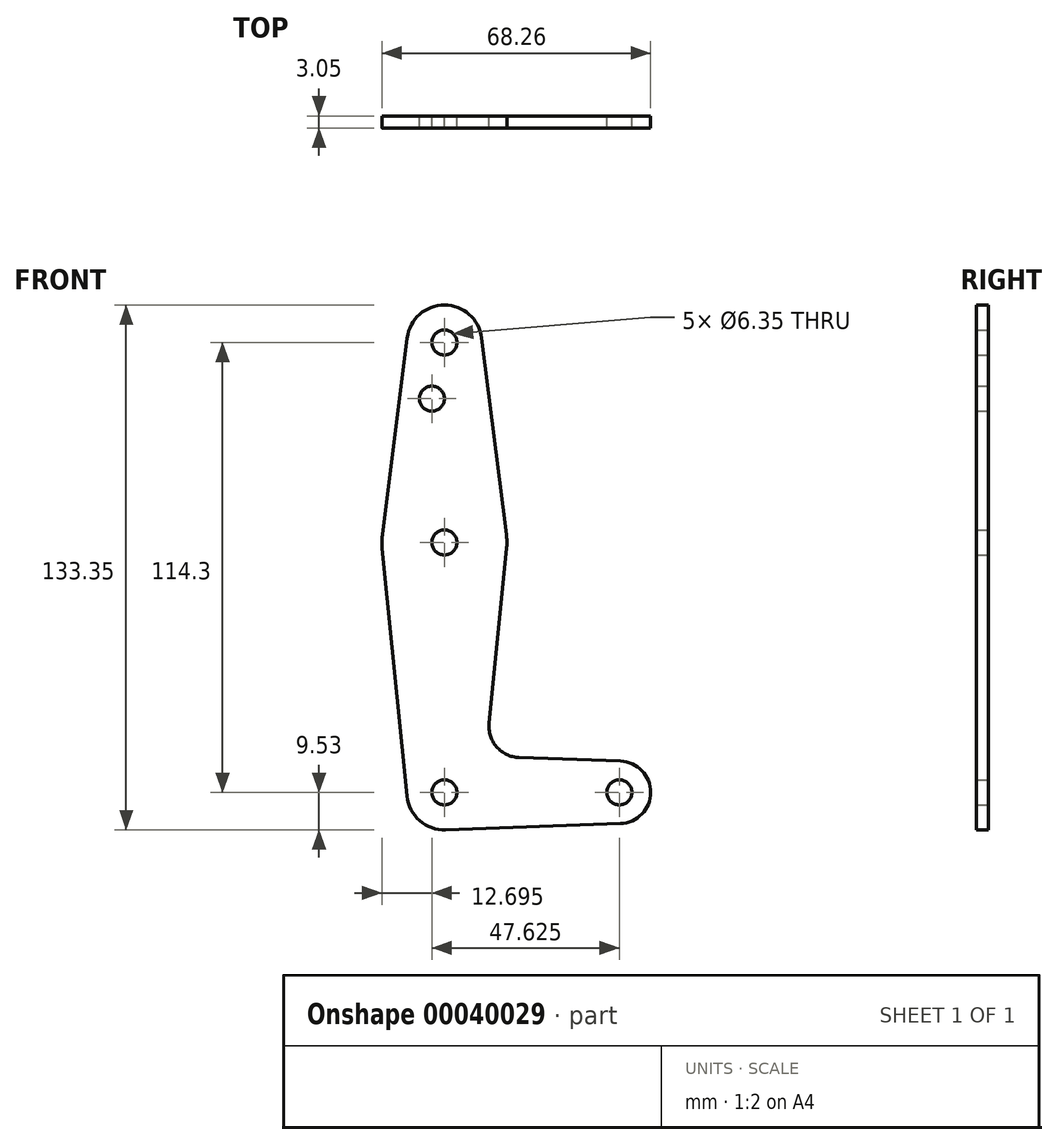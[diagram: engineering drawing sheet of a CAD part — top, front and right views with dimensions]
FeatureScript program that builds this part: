
annotation { "Feature Type Name" : "Feature", "Feature Type Description" : "" }
export const myFeature = defineFeature(function(context is Context, id is Id, definition is map)
    precondition{}
    {
        {
            var Q0;
            Q0=qCreatedBy(makeId("Front.planeOp"),FACE);
            var sketch = newSketch(context, id + "F0", { "sketchPlane" : qUnion([Q0])});
            skLineSegment(sketch, "E0", {"start": v(0, 50.8) * mm, "end": v(0, -63.5) * mm, "construction": true});
            skCircle(sketch, "E1", {"center": v(0, 50.8) * mm, "radius": 9.53 * mm});
            skCircle(sketch, "E2", {"center": v(0, 0) * mm, "radius": 15.88 * mm});
            skCircle(sketch, "E3", {"center": v(0, -63.5) * mm, "radius": 9.53 * mm});
            skLineSegment(sketch, "E4", {"start": v(0, -63.5) * mm, "end": v(44.45, -63.5) * mm, "construction": true});
            skCircle(sketch, "E5", {"center": v(44.45, -63.5) * mm, "radius": 7.94 * mm});
            skLineSegment(sketch, "E6", {"start": v(-9.45, 52) * mm, "end": v(-15.75, 1.98) * mm});
            skLineSegment(sketch, "E7", {"start": v(9.45, 52) * mm, "end": v(15.75, 1.98) * mm});
            skLineSegment(sketch, "E8", {"start": v(-15.8, -1.59) * mm, "end": v(-9.48, -64.45) * mm});
            skLineSegment(sketch, "E9", {"start": v(15.8, -1.59) * mm, "end": v(11.34, -45.9) * mm});
            skLineSegment(sketch, "E10", {"start": v(18.97, -54.65) * mm, "end": v(44.73, -55.57) * mm});
            skLineSegment(sketch, "E11", {"start": v(44.73, -71.43) * mm, "end": v(0.34, -73.02) * mm});
            skCircle(sketch, "E12", {"center": v(0, 50.8) * mm, "radius": 3.18 * mm});
            skCircle(sketch, "E13", {"center": v(-3.17, 36.53) * mm, "radius": 3.18 * mm});
            skCircle(sketch, "E14", {"center": v(0, 0) * mm, "radius": 3.18 * mm});
            skCircle(sketch, "E15", {"center": v(0, -63.5) * mm, "radius": 3.18 * mm});
            skCircle(sketch, "E16", {"center": v(44.45, -63.5) * mm, "radius": 3.18 * mm});
            skArc(sketch, "E17.filletArc", {"start": v(11.34, -45.9) * mm, "mid": v(13.26, -51.93) * mm, "end": v(18.97, -54.65) * mm});
            skSolve(sketch);
        }
        {
            var Q0;
            Q0 = qSketchRegion(id + "F0", true);
            extrude(context, id + "F1", {"entities" : qUnion([Q0]), "depth" : 3.05 * mm});
        }
    });
